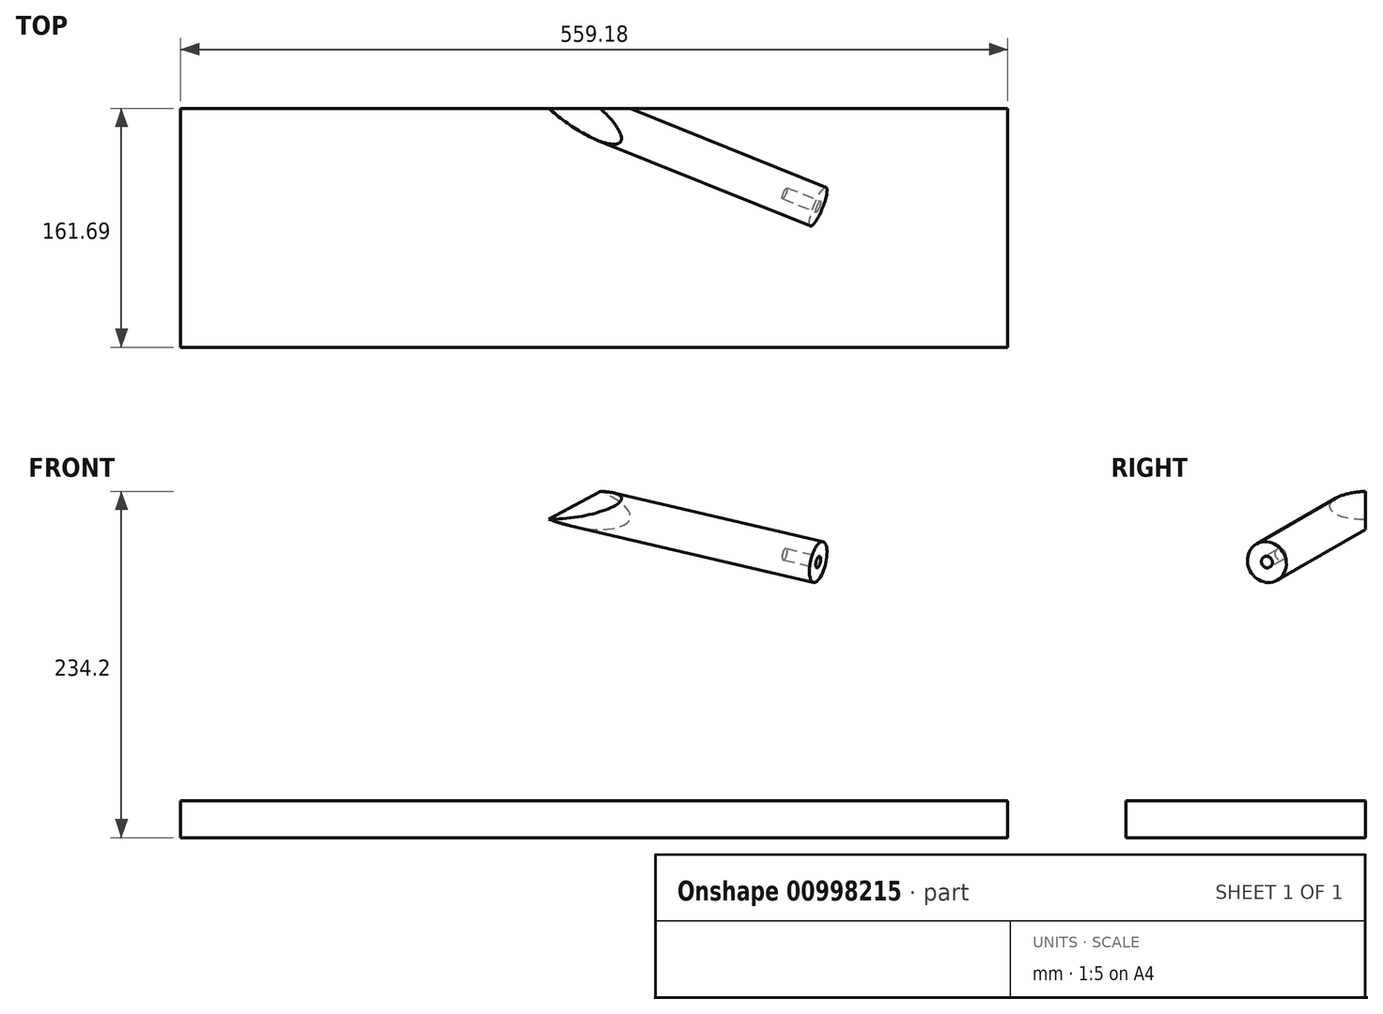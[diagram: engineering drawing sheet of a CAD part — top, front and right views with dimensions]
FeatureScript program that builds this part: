
annotation { "Feature Type Name" : "Feature", "Feature Type Description" : "" }
export const myFeature = defineFeature(function(context is Context, id is Id, definition is map)
    precondition{}
    {
        {
            var Q0;
            Q0=qCreatedBy(makeId("Top.planeOp"),FACE);
            var sketch = newSketch(context, id + "F0", { "sketchPlane" : qUnion([Q0])});
            skLineSegment(sketch, "E0", {"start": v(0, 0) * mm, "end": v(0, 143.54) * mm, "construction": true});
            skLineSegment(sketch, "E1", {"start": v(0, 0) * mm, "end": v(242.99, 0) * mm, "construction": true});
            skSolve(sketch);
        }
        {
            var Q0;
            Q0=qCreatedBy(makeId("Front.planeOp"),FACE);
            cPlane(context, id + "F1", {"entities" : qUnion([Q0]), "cplaneType" : CPlaneType.OFFSET, "offset" : 50 * mm, "oppositeDirection" : true, "width" : 150 * mm, "height" : 150 * mm});
        }
        {
            var Q0;
            Q0=qCreatedBy(id+"F1.planeOp",FACE);
            var sketch = newSketch(context, id + "F2", { "sketchPlane" : qUnion([Q0])});
            skCircle(sketch, "E2", {"center": v(0, 0) * mm, "radius": 35.27 * mm});
            skCircle(sketch, "E3", {"center": v(0, 0) * mm, "radius": 52.45 * mm});
            skSolve(sketch);
        }
        {
            var Q0;
            Q0 = qSketchRegion(id + "F2", true);
            extrude(context, id + "F3", {"entities" : qUnion([Q0]), "depth" : 10 * mm, "offsetDistance" : 25 * mm});
        }
        {
            var Q0;
            Q0=qCreatedBy(makeId("Top.planeOp"),FACE);
            var Q1;
            Q1=sQuery(id+"F0.wireOp",EDGE,"E1");
            cPlane(context, id + "F4", {"entities" : qUnion([Q0, Q1]), "cplaneType" : CPlaneType.LINE_ANGLE, "offset" : 25 * mm, "angle" : 30 * degree, "width" : 150 * mm, "height" : 150 * mm});
        }
        {
            var Q0;
            Q0=qCreatedBy(id+"F4.planeOp",FACE);
            var sketch = newSketch(context, id + "F5", { "sketchPlane" : qUnion([Q0])});
            skLineSegment(sketch, "E4", {"start": v(231.99, 0) * mm, "end": v(231.99, 16.3) * mm, "construction": true});
            skSolve(sketch);
        }
        {
            var Q0;
            Q0=sQuery(id+"F5.wireOp",EDGE,"E4");
            var Q1;
            Q1=qCreatedBy(id+"F4.planeOp",FACE);
            cPlane(context, id + "F6", {"entities" : qUnion([Q0, Q1]), "cplaneType" : CPlaneType.LINE_ANGLE, "offset" : 25 * mm, "angle" : 90 * degree, "width" : 150 * mm, "height" : 150 * mm});
        }
        {
            var Q0;
            Q0=qCreatedBy(id+"F6.planeOp",FACE);
            var sketch = newSketch(context, id + "F7", { "sketchPlane" : qUnion([Q0])});
            skLineSegment(sketch, "E5.0", {"start": v(0, 0) * mm, "end": v(14.12, -8.15) * mm, "construction": true});
            skLineSegment(sketch, "E6", {"start": v(14.12, -8.15) * mm, "end": v(28.4, 16.58) * mm, "construction": true});
            skSolve(sketch);
        }
        {
            var Q0;
            Q0=sQuery(id+"F7.wireOp",EDGE,"E6");
            var Q1;
            Q1=qCreatedBy(id+"F6.planeOp",FACE);
            cPlane(context, id + "F8", {"entities" : qUnion([Q0, Q1]), "cplaneType" : CPlaneType.LINE_ANGLE, "offset" : 25 * mm, "angle" : 25 * degree, "oppositeDirection" : true, "width" : 150 * mm, "height" : 150 * mm});
        }
        {
            var Q0;
            Q0=qCreatedBy(id+"F8.planeOp",FACE);
            var sketch = newSketch(context, id + "F9", { "sketchPlane" : qUnion([Q0])});
            skLineSegment(sketch, "E7.0", {"start": v(70.23, 44.74) * mm, "end": v(54.88, 68.83) * mm, "construction": true});
            skLineSegment(sketch, "E8.bottom", {"start": v(66.88, 78.83) * mm, "end": v(46.88, 78.83) * mm});
            skLineSegment(sketch, "E8.top", {"start": v(66.88, 58.83) * mm, "end": v(46.88, 58.83) * mm});
            skLineSegment(sketch, "E8.left", {"start": v(66.88, 78.83) * mm, "end": v(66.88, 58.83) * mm});
            skLineSegment(sketch, "E8.right", {"start": v(46.88, 78.83) * mm, "end": v(46.88, 58.83) * mm});
            skPoint(sketch, "E8.middle", {"position": v(56.88, 68.83) * mm});
            skLineSegment(sketch, "E9", {"start": v(54.88, 68.83) * mm, "end": v(56.88, 68.83) * mm, "construction": true});
            skCircle(sketch, "E10", {"center": v(56.88, 68.83) * mm, "radius": 4 * mm});
            skCircle(sketch, "E11", {"center": v(56.88, 68.83) * mm, "radius": 14.14 * mm});
            skSolve(sketch);
        }
        {
            var Q0;
            Q0=makeQuery(id+"F9.imprint","IMPRINT",FACE,{"disambiguationData":[TD([[makeQuery(id+"F9.imprint","IMPRINT",EDGE,{"derivedFrom":sQuery(id+"F9.wireOp",EDGE,"E8.bottom")}),1.0]])]});
            var Q1;
            Q1=makeQuery(id+"F9.imprint","IMPRINT",FACE,{"disambiguationData":[TD([[makeQuery(id+"F9.imprint","IMPRINT",EDGE,{"derivedFrom":sQuery(id+"F9.wireOp",EDGE,"E10")}),1.0]])]});
            var Q2;
            {var subQ0=sQuery(id+"F9.wireOp",EDGE,"E8.right");Q2=makeQuery(id+"F9.imprint","IMPRINT",FACE,{"disambiguationData":[TD([[makeQuery(id+"F9.imprint","IMPRINT",EDGE,{"derivedFrom":subQ0}),-1.0]])]});}
            var Q3;
            {var subQ0=sQuery(id+"F9.wireOp",EDGE,"E8.bottom");Q3=makeQuery(id+"F9.imprint","IMPRINT",FACE,{"disambiguationData":[TD([[makeQuery(id+"F9.imprint","IMPRINT",EDGE,{"derivedFrom":subQ0}),-1.0]])]});}
            var Q4;
            {var subQ0=sQuery(id+"F9.wireOp",EDGE,"E8.left");Q4=makeQuery(id+"F9.imprint","IMPRINT",FACE,{"disambiguationData":[TD([[makeQuery(id+"F9.imprint","IMPRINT",EDGE,{"derivedFrom":subQ0}),1.0]])]});}
            var Q5;
            {var subQ0=sQuery(id+"F9.wireOp",EDGE,"E8.top");Q5=makeQuery(id+"F9.imprint","IMPRINT",FACE,{"disambiguationData":[TD([[makeQuery(id+"F9.imprint","IMPRINT",EDGE,{"derivedFrom":subQ0}),1.0]])]});}
            extrude(context, id + "F10", {"entities" : qUnion([Q0, Q1, Q2, Q3, Q4, Q5]), "oppositeDirection" : true, "depth" : 2000 * mm, "offsetDistance" : 25 * mm});
        }
        {
            var Q0;
            Q0=makeQuery(id+"F9.imprint","IMPRINT",FACE,{"disambiguationData":[TD([[makeQuery(id+"F9.imprint","IMPRINT",EDGE,{"derivedFrom":sQuery(id+"F9.wireOp",EDGE,"E10")}),1.0]])]});
            extrude(context, id + "F11", {"entities" : qUnion([Q0]), "operationType" : NewBodyOperationType.REMOVE, "oppositeDirection" : true, "depth" : 25 * mm, "offsetDistance" : 25 * mm});
        }
        {
            var Q0;
            Q0=qCreatedBy(makeId("Top.planeOp"),FACE);
            cPlane(context, id + "F12", {"entities" : qUnion([Q0]), "cplaneType" : CPlaneType.OFFSET, "offset" : 145 * mm, "oppositeDirection" : true, "width" : 150 * mm, "height" : 150 * mm});
        }
        {
            var Q0;
            Q0=qCreatedBy(id+"F12.planeOp",FACE);
            var sketch = newSketch(context, id + "F13", { "sketchPlane" : qUnion([Q0])});
            skLineSegment(sketch, "E12.bottom", {"start": v(-198.31, -121.69) * mm, "end": v(360.87, -121.69) * mm});
            skLineSegment(sketch, "E12.top", {"start": v(-198.31, 78.82) * mm, "end": v(360.87, 78.82) * mm});
            skLineSegment(sketch, "E12.left", {"start": v(-198.31, -121.69) * mm, "end": v(-198.31, 78.82) * mm});
            skLineSegment(sketch, "E12.right", {"start": v(360.87, -121.69) * mm, "end": v(360.87, 78.82) * mm});
            skSolve(sketch);
        }
        {
            var Q0;
            Q0 = qSketchRegion(id + "F13", true);
            extrude(context, id + "F14", {"entities" : qUnion([Q0]), "oppositeDirection" : true, "depth" : 25 * mm, "offsetDistance" : 25 * mm});
        }
        {
            var Q0;
            Q0=qCreatedBy(makeId("Front.planeOp"),FACE);
            cPlane(context, id + "F15", {"entities" : qUnion([Q0]), "cplaneType" : CPlaneType.OFFSET, "offset" : 40 * mm, "oppositeDirection" : true, "width" : 150 * mm, "height" : 150 * mm});
        }
        {
            var Q0;
            Q0=qCreatedBy(id+"F15.planeOp",FACE);
            var sketch = newSketch(context, id + "F16", { "sketchPlane" : qUnion([Q0])});
            skLineSegment(sketch, "E13.bottom", {"start": v(-1972.26, -1556.68) * mm, "end": v(1915.15, -1556.68) * mm});
            skLineSegment(sketch, "E13.top", {"start": v(-1972.26, 1728.74) * mm, "end": v(1915.15, 1728.74) * mm});
            skLineSegment(sketch, "E13.left", {"start": v(-1972.26, -1556.68) * mm, "end": v(-1972.26, 1728.74) * mm});
            skLineSegment(sketch, "E13.right", {"start": v(1915.15, -1556.68) * mm, "end": v(1915.15, 1728.74) * mm});
            skSolve(sketch);
        }
        {
            var Q0;
            Q0=makeQuery(id+"F10.opExtrude","SWEPT_BODY",BODY,{"disambiguationData":[OSD([sQuery(id+"F9.wireOp",EDGE,"E11")])]});
            var Q1;
            Q1=sQuery(id+"F9.wireOp",EDGE,"E10");
            transform(context, id + "F17", {"entities" : qUnion([Q0]), "transformType" : TransformType.ROTATION, "transformAxis" : qUnion([Q1]), "angle" : 0 * degree, "oppositeDirection" : true, "makeCopy" : false});
        }
        {
            var Q0;
            Q0=makeQuery(id+"F16.imprint","IMPRINT",FACE,{"disambiguationData":[TD([[makeQuery(id+"F16.imprint","IMPRINT",EDGE,{"derivedFrom":sQuery(id+"F16.wireOp",EDGE,"E13.bottom")}),1.0]])]});
            extrude(context, id + "F18", {"entities" : qUnion([Q0]), "operationType" : NewBodyOperationType.REMOVE, "endBound" : BoundingType.THROUGH_ALL, "oppositeDirection" : true, "depth" : 25 * mm, "offsetDistance" : 25 * mm});
        }
        {
            var Q0;
            Q0=makeQuery(id+"F10.opExtrude","SWEPT_BODY",BODY,{"disambiguationData":[OSD([sQuery(id+"F9.wireOp",EDGE,"E11")])]});
            var Q1;
            Q1=sQuery(id+"F9.wireOp",EDGE,"E10");
            transform(context, id + "F19", {"entities" : qUnion([Q0]), "transformType" : TransformType.ROTATION, "transformAxis" : qUnion([Q1]), "angle" : 225 * degree, "oppositeDirection" : true, "makeCopy" : false});
        }
        {
            var Q0;
            Q0=qCreatedBy(makeId("Front.planeOp"),FACE);
            cPlane(context, id + "F20", {"entities" : qUnion([Q0]), "cplaneType" : CPlaneType.OFFSET, "offset" : 40 * mm, "oppositeDirection" : true, "width" : 150 * mm, "height" : 150 * mm});
        }
        {
            var Q0;
            Q0=qCreatedBy(id+"F20.planeOp",FACE);
            var sketch = newSketch(context, id + "F21", { "sketchPlane" : qUnion([Q0])});
            skLineSegment(sketch, "E14.0.0", {"start": v(1915.15, 1728.74) * mm, "end": v(-1972.26, 1728.74) * mm});
            skLineSegment(sketch, "E14.0.1", {"start": v(-1972.26, 1728.74) * mm, "end": v(-1972.26, -1556.68) * mm});
            skLineSegment(sketch, "E14.0.2", {"start": v(-1972.26, -1556.68) * mm, "end": v(1915.15, -1556.68) * mm});
            skLineSegment(sketch, "E14.0.3", {"start": v(1915.15, -1556.68) * mm, "end": v(1915.15, 1728.74) * mm});
            skSolve(sketch);
        }
        {
            var Q0;
            Q0=makeQuery(id+"F21.imprint","IMPRINT",FACE,{"disambiguationData":[TD([[makeQuery(id+"F21.imprint","IMPRINT",EDGE,{"derivedFrom":sQuery(id+"F21.wireOp",EDGE,"E14.0.0")}),1.0]])]});
            extrude(context, id + "F22", {"entities" : qUnion([Q0]), "operationType" : NewBodyOperationType.REMOVE, "endBound" : BoundingType.THROUGH_ALL, "oppositeDirection" : true, "depth" : 456 * mm, "offsetDistance" : 25 * mm});
        }
        {
            var Q0;
            Q0=makeQuery(id+"F9.imprint","IMPRINT",FACE,{"disambiguationData":[TD([[makeQuery(id+"F9.imprint","IMPRINT",EDGE,{"derivedFrom":sQuery(id+"F9.wireOp",EDGE,"E8.bottom")}),1.0]])]});
            cPlane(context, id + "F23", {"entities" : qUnion([Q0]), "cplaneType" : CPlaneType.OFFSET, "offset" : 25 * mm, "width" : 150 * mm, "height" : 150 * mm});
        }
        {
            var Q0;
            Q0=makeQuery(id+"F22.boolean.opBoolean","INTERSECT",EDGE,{"derivedFrom":[makeQuery(id+"F18.boolean.opBoolean","COPY",FACE,{"derivedFrom":makeQuery(id+"F18.opExtrude","CAP_FACE",FACE,{"disambiguationData":[OSD([sQuery(id+"F16.wireOp",EDGE,"E13.bottom"),sQuery(id+"F16.wireOp",EDGE,"E13.top"),sQuery(id+"F16.wireOp",EDGE,"E13.left"),sQuery(id+"F16.wireOp",EDGE,"E13.right")])],"isStart":true})}),makeQuery(id+"F22.opExtrude","CAP_FACE",FACE,{"disambiguationData":[OSD([sQuery(id+"F21.wireOp",EDGE,"E14.0.0"),sQuery(id+"F21.wireOp",EDGE,"E14.0.1"),sQuery(id+"F21.wireOp",EDGE,"E14.0.2"),sQuery(id+"F21.wireOp",EDGE,"E14.0.3")])],"isStart":true})]});
            cPlane(context, id + "F24", {"entities" : qUnion([Q0]), "cplaneType" : CPlaneType.MID_PLANE, "offset" : 25 * mm, "width" : 150 * mm, "height" : 150 * mm});
        }
    });
